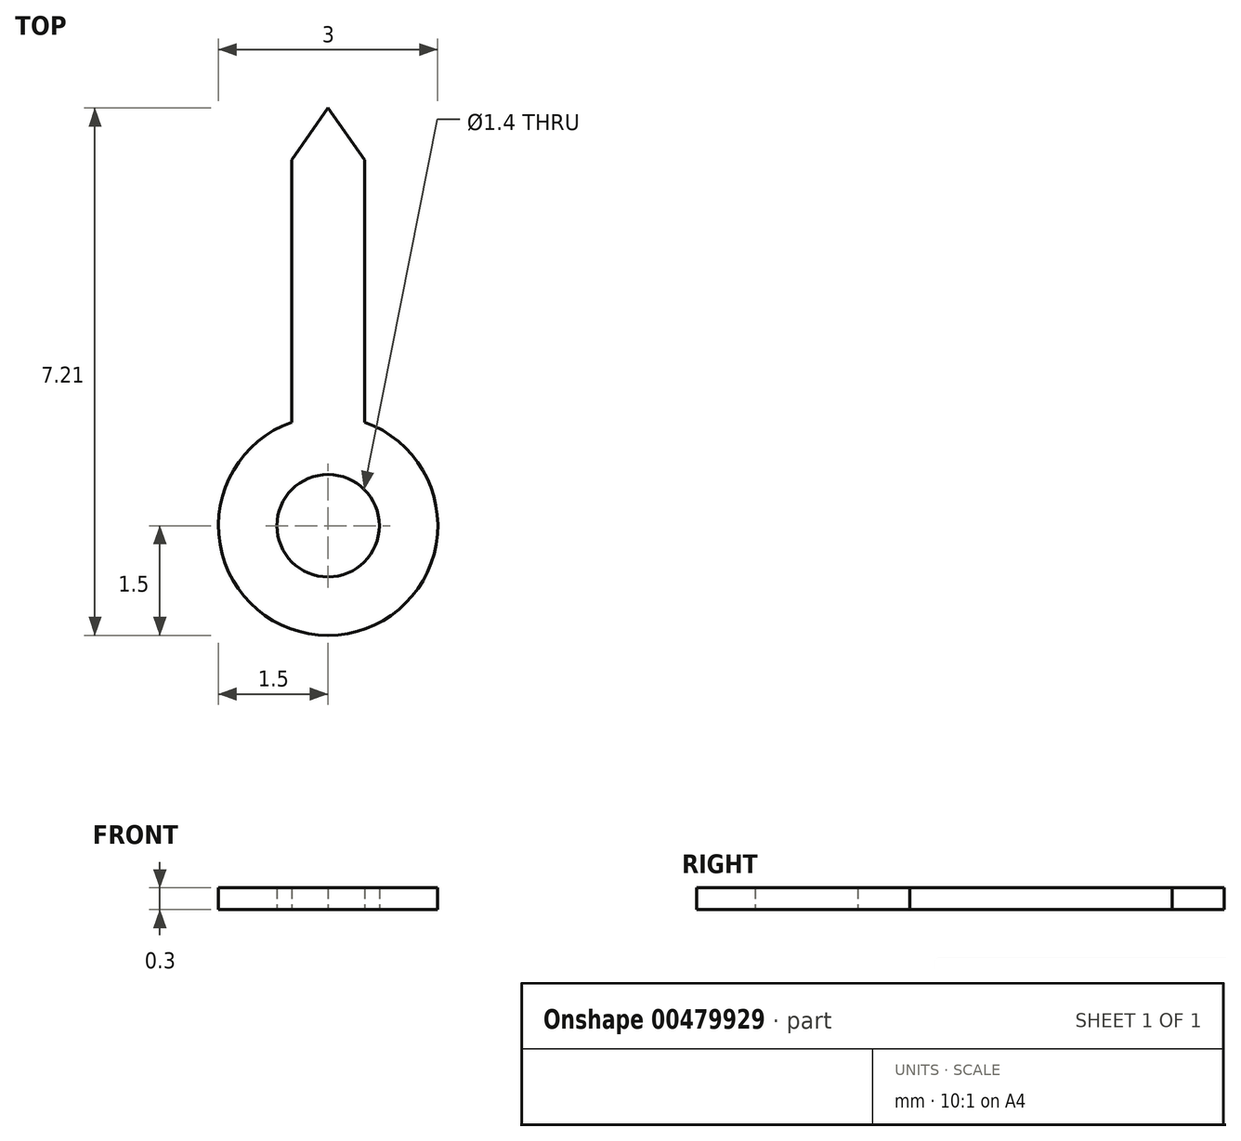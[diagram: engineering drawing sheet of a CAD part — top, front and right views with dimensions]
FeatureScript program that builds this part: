
annotation { "Feature Type Name" : "Feature", "Feature Type Description" : "" }
export const myFeature = defineFeature(function(context is Context, id is Id, definition is map)
    precondition{}
    {
        {
            var Q0;
            Q0=qCreatedBy(makeId("Top.planeOp"),FACE);
            var sketch = newSketch(context, id + "F0", { "sketchPlane" : qUnion([Q0])});
            skCircle(sketch, "E0", {"center": v(0, 0) * mm, "radius": 1.5 * mm});
            skLineSegment(sketch, "E1.bottom", {"start": v(-0.5, 0) * mm, "end": v(0.5, 0) * mm});
            skLineSegment(sketch, "E1.top", {"start": v(-0.5, 5) * mm, "end": v(0.5, 5) * mm});
            skLineSegment(sketch, "E1.left", {"start": v(-0.5, 0) * mm, "end": v(-0.5, 5) * mm});
            skLineSegment(sketch, "E1.right", {"start": v(0.5, 0) * mm, "end": v(0.5, 5) * mm});
            skLineSegment(sketch, "E2", {"start": v(-0.5, 5) * mm, "end": v(0, 5.71) * mm});
            skLineSegment(sketch, "E3", {"start": v(0, 5.71) * mm, "end": v(0.5, 5) * mm});
            skSolve(sketch);
        }
        {
            var Q0;
            {var subQ5=sQuery(id+"F0.wireOp",EDGE,"E1.top");Q0=makeQuery(id+"F0.imprint","IMPRINT",FACE,{"disambiguationData":[TD([[makeQuery(id+"F0.imprint","IMPRINT",EDGE,{"derivedFrom":subQ5}),-1.0]])]});}
            var Q1;
            Q1=makeQuery(id+"F0.imprint","IMPRINT",FACE,{"disambiguationData":[TD([[makeQuery(id+"F0.imprint","IMPRINT",EDGE,{"derivedFrom":sQuery(id+"F0.wireOp",EDGE,"E1.top")}),1.0]])]});
            var Q2;
            {var subQ5=sQuery(id+"F0.wireOp",EDGE,"E1.bottom");Q2=makeQuery(id+"F0.imprint","IMPRINT",FACE,{"disambiguationData":[TD([[makeQuery(id+"F0.imprint","IMPRINT",EDGE,{"derivedFrom":subQ5}),1.0]])]});}
            var Q3;
            {var subQ5=sQuery(id+"F0.wireOp",EDGE,"E1.bottom");Q3=makeQuery(id+"F0.imprint","IMPRINT",FACE,{"disambiguationData":[TD([[makeQuery(id+"F0.imprint","IMPRINT",EDGE,{"derivedFrom":subQ5}),-1.0]])]});}
            extrude(context, id + "F1", {"entities" : qUnion([Q0, Q1, Q2, Q3]), "depth" : 0.3 * mm});
        }
        {
            var Q0;
            Q0=makeQuery(id+"F1.opExtrude","CAP_FACE",FACE,{"disambiguationData":[OSD([sQuery(id+"F0.wireOp",EDGE,"E0"),sQuery(id+"F0.wireOp",EDGE,"E1.left"),sQuery(id+"F0.wireOp",EDGE,"E1.right"),sQuery(id+"F0.wireOp",EDGE,"E2"),sQuery(id+"F0.wireOp",EDGE,"E3")])],"isStart":false});
            var sketch = newSketch(context, id + "F2", { "sketchPlane" : qUnion([Q0])});
            skCircle(sketch, "E4", {"center": v(0, 0) * mm, "radius": 0.7 * mm});
            skSolve(sketch);
        }
        {
            var Q0;
            Q0=makeQuery(id+"F2.imprint","IMPRINT",FACE,{"disambiguationData":[TD([[makeQuery(id+"F2.imprint","IMPRINT",EDGE,{"derivedFrom":sQuery(id+"F2.wireOp",EDGE,"E4")}),1.0]])]});
            extrude(context, id + "F3", {"entities" : qUnion([Q0]), "operationType" : NewBodyOperationType.REMOVE, "endBound" : BoundingType.SYMMETRIC, "depth" : 25 * mm});
        }
    });
